# Revit family: R1220-EU
name_source: partatom
category: Plumbing Fixtures
revit_build: Autodesk Revit 2018 (Build: 20170223_1515(x64)
units: mm (PartAtom-declared; Revit-internal decimal feet)

## family parameters
Cut with Voids When Loaded = No
Host = Face
Part Type = Normal
Room Calculation Point = No
Round Connector Dimension = Use Radius
Shared = No

## types (4) — shared parameters
Adjustable cast iron extension deck flange = 0' - 5"
Adjustment Height = 0' - 8"
Body Height = 0' - 4 1/2"
Default Elevation = 0' - 0"
Description = MEDIUM SUMP EXTENSION ROOF DRAIN FOR 1 3/4” TO 7” INSULATION
Domestic Cold Water Diameter = 0' - 0 1/2"
Domestic Cold Water Radius = 0' - 0 1/2"
Floor Drain Material = Paint - Sherwin Williams Paint - #952C2A - Bellwood Red
Manufacturer = MIFAB
Model = R1220-EU
Strainer Diameter = 0' - 7"
URL = WWW.MIFAB.COM
zero-valued in all types: CWFU, WFU

## per-type parameters (varying)
| type | Pipe Diameter | Pipe Radius |
| 6" Drain Pipe Size | 0' - 6" | 0' - 3" |
| 4" Drain Pipe Size | 0' - 4" | 0' - 2" |
| 3" Drain Pipe Size | 0' - 3" | 0' - 1 1/2" |
| 2" Drain Pipe Size | 0' - 2" | 0' - 1" |

## geometry (parser evidence)
native form markers: Blend x2, Sweep x9
no freeform markers — native parametric forms only
